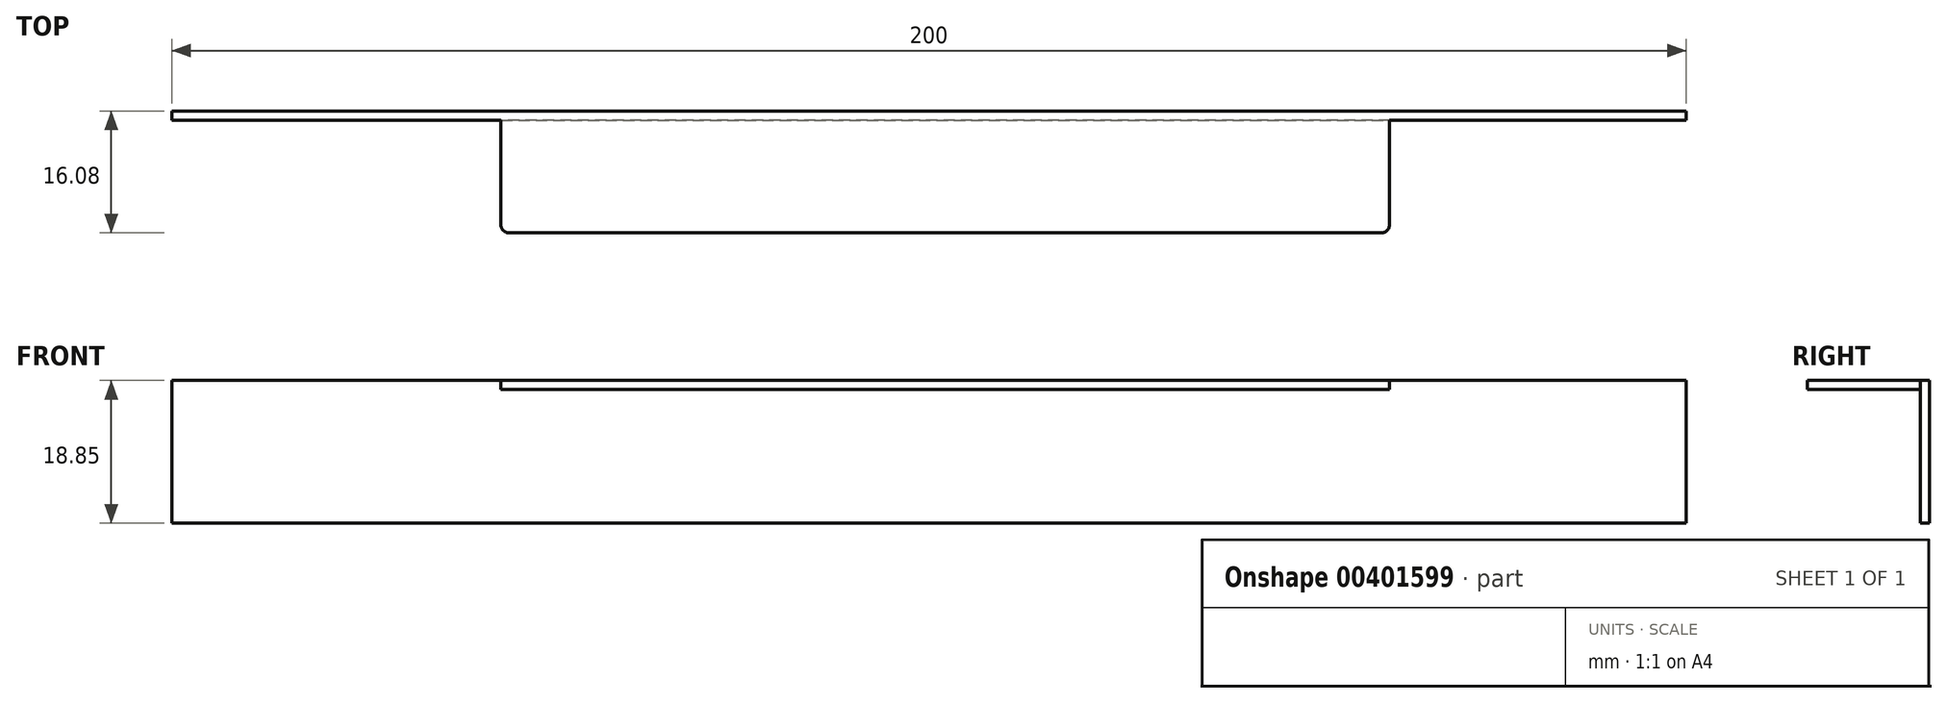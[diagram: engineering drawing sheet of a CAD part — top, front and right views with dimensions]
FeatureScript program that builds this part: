
annotation { "Feature Type Name" : "Feature", "Feature Type Description" : "" }
export const myFeature = defineFeature(function(context is Context, id is Id, definition is map)
    precondition{}
    {
        {
            var Q0;
            Q0=qCreatedBy(makeId("Top.planeOp"),FACE);
            var sketch = newSketch(context, id + "F0", { "sketchPlane" : qUnion([Q0])});
            skLineSegment(sketch, "E0.bottom", {"start": v(-56.53, 0) * mm, "end": v(60.78, 0) * mm});
            skLineSegment(sketch, "E0.top", {"start": v(-56.53, -14.88) * mm, "end": v(60.78, -14.88) * mm});
            skLineSegment(sketch, "E0.left", {"start": v(-56.53, 0) * mm, "end": v(-56.53, -14.88) * mm});
            skLineSegment(sketch, "E0.right", {"start": v(60.78, 0) * mm, "end": v(60.78, -14.88) * mm});
            skSolve(sketch);
        }
        {
            var Q0;
            Q0=makeQuery(id+"F0.imprint","IMPRINT",FACE,{"disambiguationData":[TD([[makeQuery(id+"F0.imprint","IMPRINT",EDGE,{"derivedFrom":sQuery(id+"F0.wireOp",EDGE,"E0.bottom")}),-1.0]])]});
            extrude(context, id + "F1", {"entities" : qUnion([Q0]), "oppositeDirection" : true, "depth" : 1.2 * mm});
        }
        {
            var Q0;
            Q0=makeQuery(id+"F1.opExtrude","SWEPT_EDGE",EDGE,{"disambiguationData":[OSD([sQuery(id+"F0.wireOp",EDGE,"E0.top"),sQuery(id+"F0.wireOp",EDGE,"E0.left")])]});
            var Q1;
            Q1=makeQuery(id+"F1.opExtrude","SWEPT_EDGE",EDGE,{"disambiguationData":[OSD([sQuery(id+"F0.wireOp",EDGE,"E0.top"),sQuery(id+"F0.wireOp",EDGE,"E0.right")])]});
            fillet(context, id + "F2", {"entities" : qUnion([Q0, Q1]), "radius" : 1 * mm, "tangentPropagation" : true, "allowEdgeOverflow" : false});
        }
        {
            var Q0;
            Q0=makeQuery(id+"F1.opExtrude","SWEPT_FACE",FACE,{"disambiguationData":[OSD([sQuery(id+"F0.wireOp",EDGE,"E0.bottom")])]});
            var sketch = newSketch(context, id + "F3", { "sketchPlane" : qUnion([Q0])});
            skLineSegment(sketch, "E1", {"start": v(0, 0) * mm, "end": v(-100, 0) * mm});
            skLineSegment(sketch, "E2", {"start": v(0, 0) * mm, "end": v(100, 0) * mm});
            skLineSegment(sketch, "E3.bottom", {"start": v(-100, 0) * mm, "end": v(100, 0) * mm});
            skLineSegment(sketch, "E3.top", {"start": v(-100, -18.85) * mm, "end": v(100, -18.85) * mm});
            skLineSegment(sketch, "E3.left", {"start": v(-100, 0) * mm, "end": v(-100, -18.85) * mm});
            skLineSegment(sketch, "E3.right", {"start": v(100, 0) * mm, "end": v(100, -18.85) * mm});
            skSolve(sketch);
        }
        {
            var Q0;
            Q0=makeQuery(id+"F3.imprint","IMPRINT",FACE,{"disambiguationData":[TD([[makeQuery(id+"F3.imprint","IMPRINT",EDGE,{"derivedFrom":sQuery(id+"F3.wireOp",EDGE,"E3.top")}),1.0]])]});
            var Q1;
            {var subQ1=sQuery(id+"F0.wireOp",EDGE,"E0.bottom");Q1=makeQuery(id+"F3.imprint","IMPRINT",FACE,{"disambiguationData":[TD([[makeQuery(id+"F3.imprint","IMPRINT",EDGE,{"derivedFrom":makeQuery(id+"F1.opExtrude","CAP_EDGE",EDGE,{"disambiguationData":[OSD([subQ1])],"isStart":false})}),-1.0]])]});}
            extrude(context, id + "F4", {"entities" : qUnion([Q0, Q1]), "operationType" : NewBodyOperationType.ADD, "depth" : 1.2 * mm});
        }
    });
